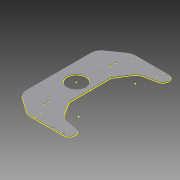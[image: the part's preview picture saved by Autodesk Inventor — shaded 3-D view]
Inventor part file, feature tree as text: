
AUTODESK INVENTOR PART (.ipt)
format: ipt  version: 2013 (Build 170138000, 138)  size: 401,920 bytes
history: native  units: mm
features: extrude x2, sketch x2, other x1
ambient origin geometry x8: Origin, YZ Plane, XZ Plane, XY Plane, X Axis, Y Axis, Z Axis, Center Point
feature tree (5):
  extrude  "Extrusion7"  Depth=50.0mm
  extrude  "Extrusion8"  Depth=100.0mm
  sketch  "Sketch18"  dims[d5=200.0mm d6=100.0mm d7=70.0mm d8=180.0mm d9=20.0mm d10=100.0mm d11=50.0mm d14=50.0mm d15=25.0mm d16=5.0mm d17=5.0mm d18=150.0mm d19=5.0mm d20=5.0mm d21=30.0mm d22=10.0mm d23=6.0mm d24=97.0mm d25=73.0mm d26=4.0mm d27=8.0mm d28=8.0mm d29=7.0mm d30=4.0mm d31=8.0mm d33=8.0mm d34=1.0mm d35=8.0mm d36=4.0mm d37=7.0mm d38=8.0mm d39=4.0mm d40=8.0mm d41=30.0mm d42=8.0mm d43=1.0mm d61=30.0mm d89=8.0mm d90=4.0mm d91=8.0mm d92=4.0mm d93=30.0mm d95=7.0mm d96=5.0mm d97=8.0mm d98=4.0mm d99=8.0mm d100=4.0mm d101=30.0mm d103=7.0mm d104=5.0mm d114=90.0mm d127=97.0mm d128=6.0mm d129=10.0mm d130=73.0mm d131=65.0mm d132=100.0mm d133=200.0mm d134=5.0mm d135=2.5mm d136=50.0mm d137=2.5mm d150=5.0mm d151=5.0mm d152=50.0mm d153=5.0mm d154=5.0mm d155=50.0mm d162=5.0mm d163=5.0mm d164=50.0mm d165=5.0mm d166=5.0mm d167=50.0mm d182=10.0mm d183=6.0mm d184=10.0mm d185=10.0mm d186=10.0mm d187=6.0mm d195=3.0mm d196=0.0mm d197=0.5mm d199=10.0mm d200=10.0mm d201=60.0mm d202=10.0mm d203=0.5mm d204=99.75mm d205=10.0mm d206=10.0mm d207=0.5mm d208=0.5mm d209=60.0mm d210=99.75mm d211=2.0mm d212=0.0mm]
  other  "Profile"
  sketch  "Sketch17"  dims[d1=80.0mm d2=50.0mm]
